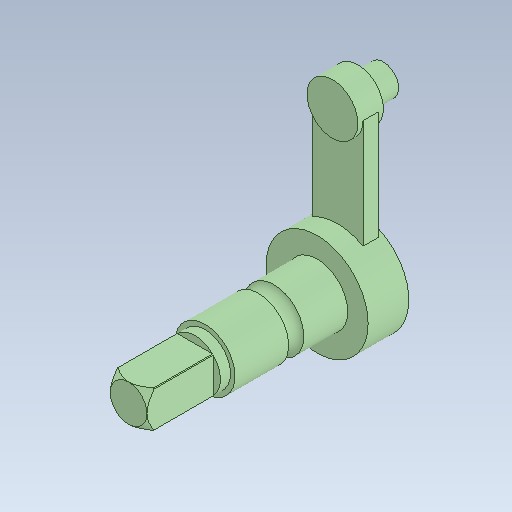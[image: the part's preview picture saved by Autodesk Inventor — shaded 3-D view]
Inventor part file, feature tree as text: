
AUTODESK INVENTOR PART (.ipt)
format: ipt  version: 2020.5 (Build 245400000, 400)  size: 200,704 bytes
history: native  units: mm
features: sketch x8, extrude x7, other x2, mirror x1, chamfer x1, revolve x1
ambient origin geometry x8: Origin, YZ Plane, XZ Plane, XY Plane, X Axis, Y Axis, Z Axis, Center Point
bodies: Solid1 (feature_tree)
feature tree (20):
  extrude  "Extrusion1"  Depth=6.0mm
  extrude  "Extrusion2"  Depth=10.0mm
  mirror  "Mirror1"
  extrude  "Extrusion3"  Depth=5.0mm TaperAngle=0.0deg
  extrude  "Extrusion4"  Depth=3.0mm TaperAngle=0.0deg
  extrude  "Extrusion5"  Depth=30.0mm TaperAngle=0.0deg
  extrude  "Extrusion6"  Depth=5.0mm TaperAngle=0.0deg
  chamfer  "Chamfer1"  Distance=15.0mm
  extrude  "Extrusion7"  Depth=13.0mm TaperAngle=0.0deg
  other  "Work Point1"
  sketch  "Sketch8"  dims[d18=10.0mm d19=15.0mm d20=0.0mm]
  revolve  "Revolution1"  [1 undecoded]
  sketch  "Sketch1"  dims[d0=30.0mm d1=6.0mm]
  sketch  "Sketch2"  dims[d2=10.0mm d3=12.0mm]
  sketch  "Sketch3"  dims[d4=20.0mm d6=5.0mm d7=0.0mm]
  sketch  "Sketch4"  dims[d8=1.0mm d9=0.0mm d10=3.0mm d11=0.0mm]
  sketch  "Sketch5"  dims[d12=0.1mm d13=30.0mm d14=0.0mm]
  sketch  "Sketch6"  dims[d15=6.0mm d16=5.0mm d17=0.0mm]
  other  "Work Axis1"
  sketch  "Sketch9"  dims[d21=1.4mm d22=2.0mm d23=45.0deg d24=13.0mm d25=0.0mm d26=3.0mm d27=12.0mm d28=90.0deg]
note: 1 required parameter value undecoded (feature->parameter linkage not recoverable at this tier; creation-order binding heuristic only, values carry confidence <= 0.55)
